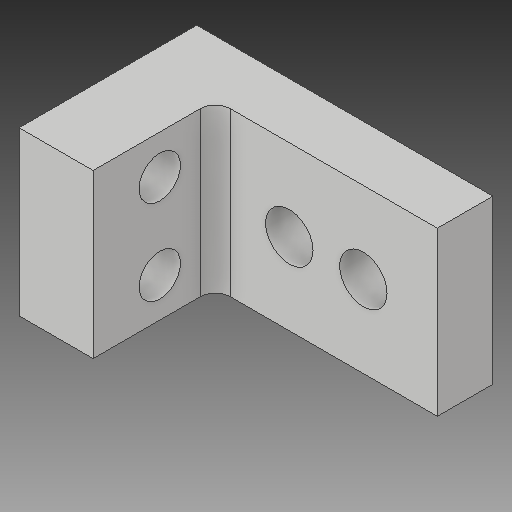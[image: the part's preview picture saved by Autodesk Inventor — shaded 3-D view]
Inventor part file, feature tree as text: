
AUTODESK INVENTOR PART (.ipt)
format: ipt  version: 2019 (Build 230136000, 136)  size: 142,336 bytes
history: native  units: in
note: dims shown in document units (in); Inventor stores cm internally (conversion verified against a paired STEP export)
features: sketch x4, extrude x2, hole x2, fillet x1
ambient origin geometry x8: Origin, YZ Plane, XZ Plane, XY Plane, X Axis, Y Axis, Z Axis, Center Point
bodies: Solid1 (feature_tree)
feature tree (9):
  extrude  "Extrusion1"  Depth=0.6in
  extrude  "Extrusion2"  Depth=0.1875in
  hole  "Hole1"  [1 undecoded]
  fillet  "Fillet1"  Radius=0.25in
  hole  "Hole2"  [1 undecoded]
  sketch  "Sketch1"  dims[d0=0.55in d1=0.6in]
  sketch  "Sketch2"  dims[d2=0.25in d3=0.0in d4=0.1875in]
  sketch  "Sketch3"  dims[d5=0.75in d6=0.0in]
  sketch  "Sketch4"  dims[d10=0.14in d11=0.75in d12=0.375in d13=0.25in d14=0.5635in d15=1.0in d16=0.8108in d17=0.05in d19=0.25in d20=0.25in d21=0.16in d22=0.75in d23=0.375in d24=0.25in d25=0.5635in d26=1.0in d27=0.8108in d28=0.375in d29=0.375in d30=0.287in d31=0.1315in d32=0.55in]
note: 2 required parameter values undecoded (feature->parameter linkage not recoverable at this tier; creation-order binding heuristic only, values carry confidence <= 0.55)
